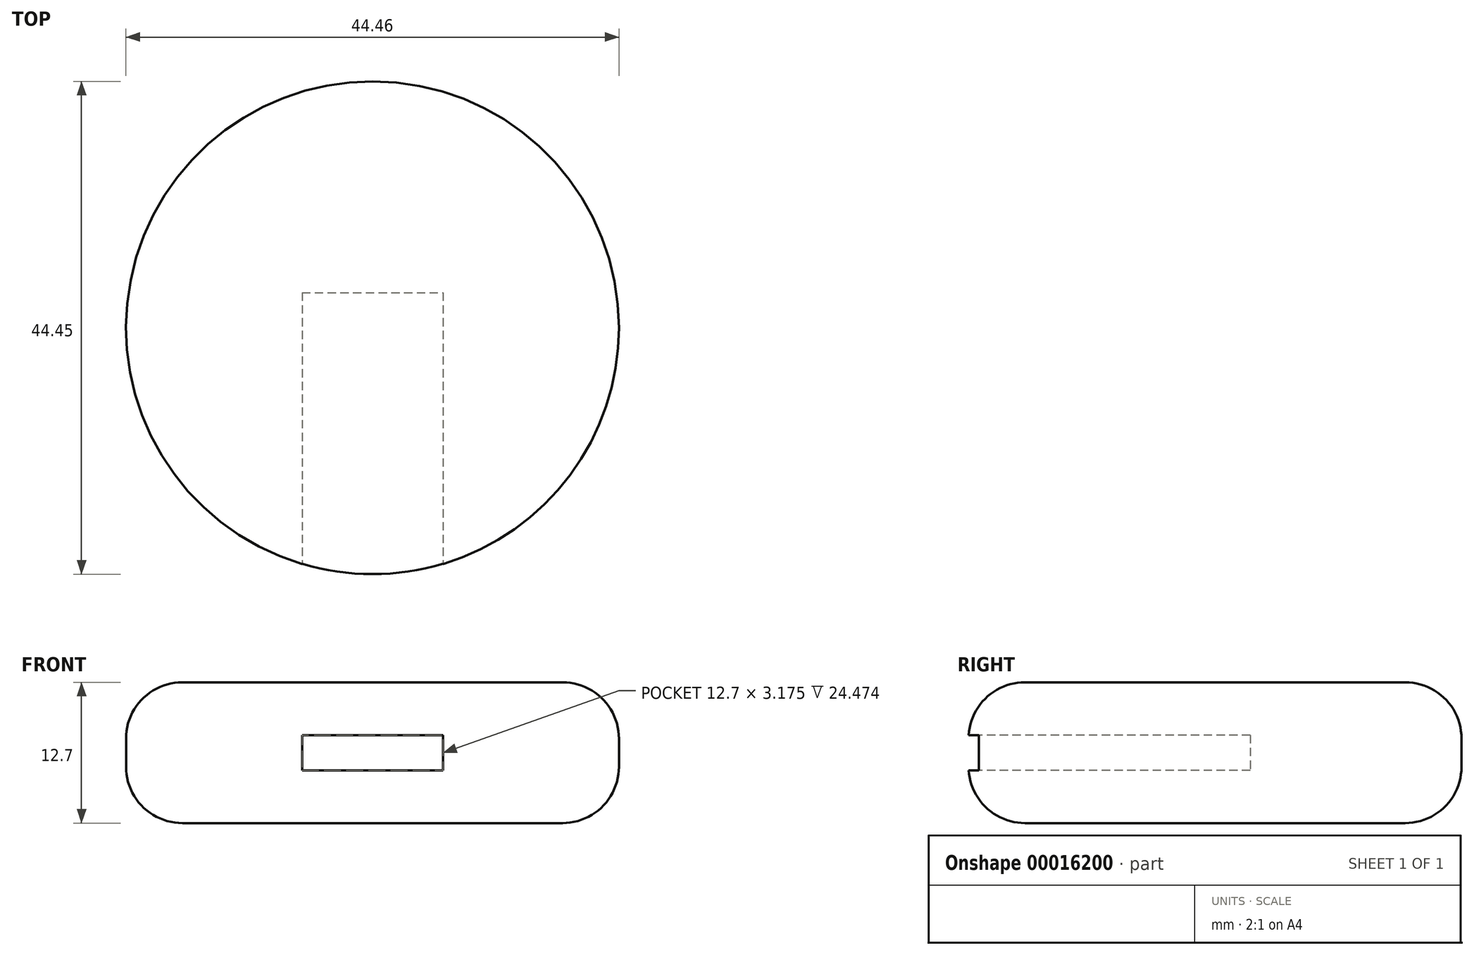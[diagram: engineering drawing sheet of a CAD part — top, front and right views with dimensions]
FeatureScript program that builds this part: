
annotation { "Feature Type Name" : "Feature", "Feature Type Description" : "" }
export const myFeature = defineFeature(function(context is Context, id is Id, definition is map)
    precondition{}
    {
        {
            var Q0;
            Q0=qCreatedBy(makeId("Top.planeOp"),FACE);
            var sketch = newSketch(context, id + "F0", { "sketchPlane" : qUnion([Q0])});
            skCircle(sketch, "E0", {"center": v(0, 0) * mm, "radius": 22.23 * mm});
            skLineSegment(sketch, "E1", {"start": v(0, 0) * mm, "end": v(0, -22.23) * mm});
            skLineSegment(sketch, "E2", {"start": v(0, -22.23) * mm, "end": v(-25.94, -22.23) * mm});
            skLineSegment(sketch, "E3", {"start": v(0, -22.23) * mm, "end": v(26.04, -22.23) * mm});
            skSolve(sketch);
        }
        {
            var Q0;
            Q0=makeQuery(id+"F0.imprint","IMPRINT",FACE,{"disambiguationData":[TD([[makeQuery(id+"F0.imprint","IMPRINT",EDGE,{"derivedFrom":sQuery(id+"F0.wireOp",EDGE,"E0")}),1.0]])]});
            extrude(context, id + "F1", {"entities" : qUnion([Q0]), "endBound" : BoundingType.SYMMETRIC, "depth" : 12.7 * mm});
        }
        {
            var Q0;
            Q0=sQuery(id+"F0.wireOp",EDGE,"E2");
            cPlane(context, id + "F2", {"entities" : qUnion([Q0]), "cplaneType" : CPlaneType.LINE_ANGLE, "offset" : 152.4 * mm, "angle" : 180 * degree, "width" : 152.4 * mm, "height" : 152.4 * mm});
        }
        {
            var Q0;
            Q0=qCreatedBy(id+"F2.planeOp",FACE);
            var sketch = newSketch(context, id + "F3", { "sketchPlane" : qUnion([Q0])});
            skLineSegment(sketch, "E4.rect.bottom", {"start": v(6.35, 1.59) * mm, "end": v(-6.35, 1.59) * mm});
            skLineSegment(sketch, "E4.rect.top", {"start": v(6.35, -1.59) * mm, "end": v(-6.35, -1.59) * mm});
            skLineSegment(sketch, "E4.rect.left", {"start": v(6.35, 1.59) * mm, "end": v(6.35, -1.59) * mm});
            skLineSegment(sketch, "E4.rect.right", {"start": v(-6.35, 1.59) * mm, "end": v(-6.35, -1.59) * mm});
            skPoint(sketch, "E4.rect.middle", {"position": v(0, 0) * mm});
            skSolve(sketch);
        }
        {
            var Q0;
            Q0=makeQuery(id+"F3.imprint","IMPRINT",FACE,{"disambiguationData":[TD([[makeQuery(id+"F3.imprint","IMPRINT",EDGE,{"derivedFrom":sQuery(id+"F3.wireOp",EDGE,"E4.rect.bottom")}),1.0]])]});
            extrude(context, id + "F4", {"entities" : qUnion([Q0]), "operationType" : NewBodyOperationType.REMOVE, "depth" : 25.4 * mm});
        }
        {
            var Q0;
            Q0=makeQuery(id+"F1.opExtrude","CAP_EDGE",EDGE,{"disambiguationData":[OSD([sQuery(id+"F0.wireOp",EDGE,"E0")])],"isStart":false});
            var Q1;
            Q1=makeQuery(id+"F1.opExtrude","CAP_EDGE",EDGE,{"disambiguationData":[OSD([sQuery(id+"F0.wireOp",EDGE,"E0")])],"isStart":true});
            fillet(context, id + "F5", {"entities" : qUnion([Q0, Q1]), "radius" : 5.08 * mm, "tangentPropagation" : true, "allowEdgeOverflow" : false});
        }
    });
